# Revit family: Sink-Undercounter-Kohler-Ladena-2214
name_source: partatom
category: Plumbing Fixtures
revit_build: Autodesk Revit 2014 (Build: 20130709_2115(x64)
units: mm (PartAtom-declared; Revit-internal decimal feet)

## types (14) — shared parameters
Assembly Code = D2010400
Default Elevation = 0' - 0"
Description = Ladena® undercounter lavatory, 18 inch x 12 inch
Height = 0' - 8 1/8"
Length = 1' - 2 3/8"
Manufacturer = Kohler
Model = K-2214
Product Documentation Link = http://www.us.kohler.com
Product Page URL = http://www.us.kohler.com
Sanitary Connector = Sanitary Connection
Sanitary Radius = 1"
URL = http://www.us.kohler.com
Waste Connection = Yes
Width = 1' - 8 7/8"
zero-valued in all types: WFU

## per-type parameters (varying)
| type | Finish | Sanitary Diameter |
| Vitreous_China-0-White | Vitreous China-Kohler-0-White | 1" |
| Vitreous_China-6-Skylight | Vitreous China-Kohler-6-Skylight | 2" |
| Vitreous_China-7-Black_Black | Vitreous China-Kohler-7-Black Black | 2" |
| Vitreous_China-33-Mexican_Sand | Vitreous China-Kohler-33-Mexican Sand | 2" |
| Vitreous_China-47-Almond | Vitreous China-Kohler-47-Almond | 2" |
| Vitreous_China-55-Innocent_Blush | Vitreous China-Kohler-55-Innocent Blush | 2" |
| Vitreous_China-58-Thunder_Grey | Vitreous China-Kohler-58-Thunder Grey | 2" |
| Vitreous_China-95-Ice_Grey | Vitreous China-Kohler-95-Ice Grey | 2" |
| Vitreous_China-96-Biscuit | Vitreous China-Kohler-96-Biscuit | 2" |
| Vitreous_China-G9-Sandbar | Vitreous China-Kohler-G9-Sandbar | 2" |
| Vitreous_China-HW1-Honed_White | Vitreous China-Kohler-HW1-Honed White | 2" |
| Vitreous_China-K4-Cashmere | Vitreous China-Kohler-K4-Cashmere | 2" |
| Vitreous_China-NG-Tea_Green | Vitreous China-Kohler-NG-Tea Green | 2" |
| Vitreous_China-Y2-Sunlight | Vitreous China-Kohler-Y2-Sunlight | 2" |

## geometry (parser evidence)
native form markers: Blend x48, Sweep x2
no freeform markers — native parametric forms only
